# Revit family: Waterstry_Фильтр_Умягчитель_F41 MF 4872 RM
name_source: partatom
category: Оборудование
units: mm (PartAtom-declared; Revit-internal decimal feet)

## family parameters
Всегда вертикально = Да
Классификация = Нет
На основе рабочей плоскости = Нет
Общий = Нет
При загрузке вырезать с полостями = Нет
Размер круглого соединителя = Использовать диаметр
Тип детали = Нормальный
Точка расчета площади = Нет

## types (1)
- WATERSTRY F41 MF 4872 RM
    ADSK_URL страницы изделия = https://waterstry.ru
    ADSK_Версия Revit = 2019.2
    ADSK_Единица измерения = шт.
    ADSK_Завод-изготовитель = WATERSTRY
    ADSK_Классификация нагрузок = ОВК
    ADSK_Количество = 1
    ADSK_Количество фаз = 1
    ADSK_Коэффициент мощности = 1
    ADSK_Марка = WATERSTRY F41 MF 4872 RM
    ADSK_Масса = 3183
    ADSK_Масса_Текст = 3183
    ADSK_Материал = Waterstry_Бежевый_Условный
    ADSK_Наименование = Автоматический фильтр-умягчитель (21,0 м. куб./ час) с солевым баком 1000л и клапаном управления Fobrite F41
    ADSK_Напряжение = 230 В
    ADSK_Номинальная мощность = 0.06 кВт
    ADSK_Полная мощность = 0.06 кВ·А
    ADSK_Размер_Высота = 2095 мм
    ADSK_Размер_Глубина = 1218 мм
    ADSK_Размер_Ширина = 1218 мм
    URL = https://waterstry.ru
    Высота баллона = 1850 мм
    Высота основания = 480 мм
    Диаметр баллона = 1218 мм
    Диаметр дренажа = 50 мм
    Диаметр присоединения = 50 мм
    Диаметр солезаборной линии = 25 мм
    Изготовитель = WATERSTRY
    Масса заполненного водой фильтра = 3183
    Масса фильтра с засыпкой = 1563
